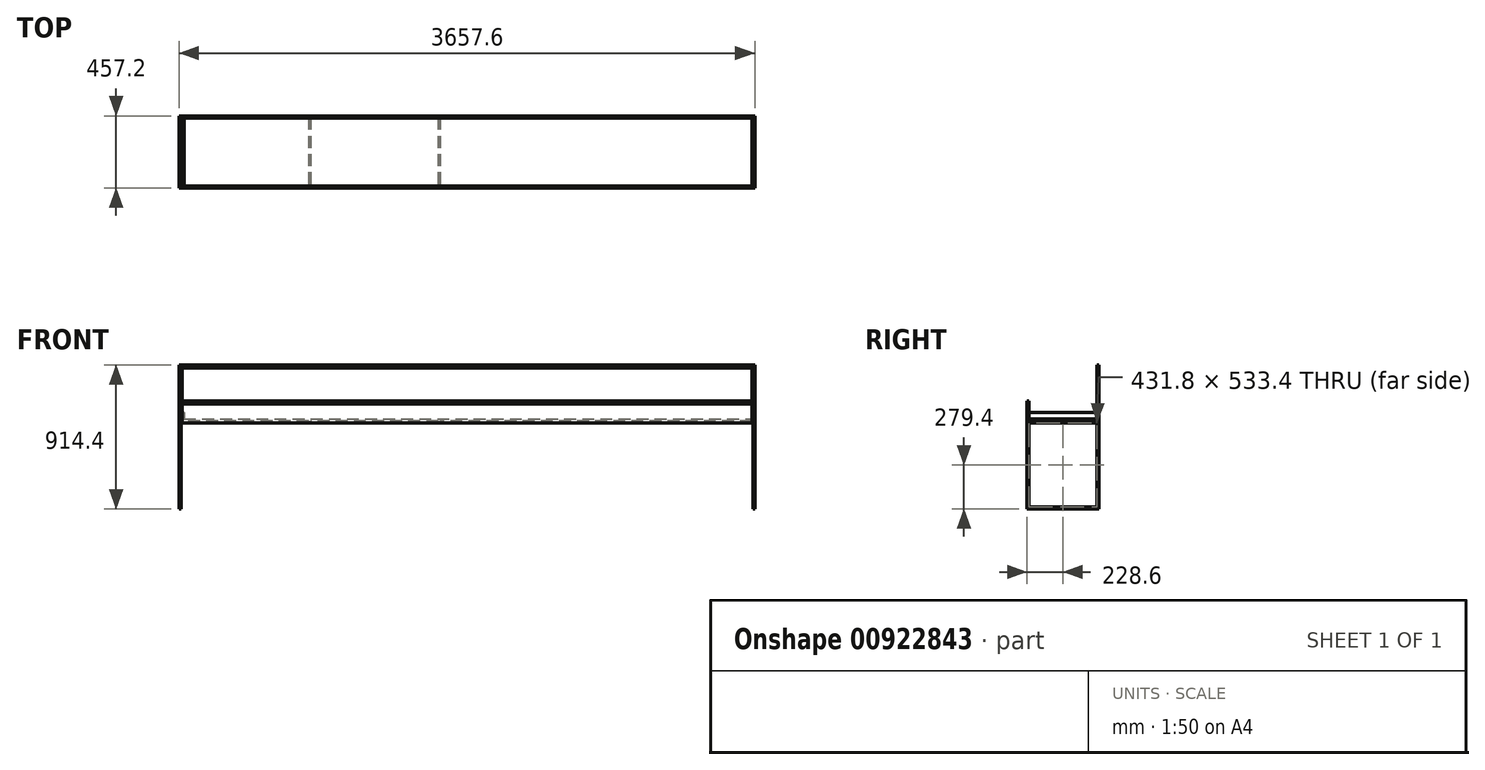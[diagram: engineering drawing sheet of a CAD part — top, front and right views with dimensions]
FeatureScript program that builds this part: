
annotation { "Feature Type Name" : "Feature", "Feature Type Description" : "" }
export const myFeature = defineFeature(function(context is Context, id is Id, definition is map)
    precondition{}
    {
        {
            var Q0;
            Q0=qCreatedBy(makeId("Front.planeOp"),FACE);
            var sketch = newSketch(context, id + "F0", { "sketchPlane" : qUnion([Q0])});
            skLineSegment(sketch, "E0.bottom", {"start": v(-2785.08, 0) * mm, "end": v(872.52, 0) * mm});
            skLineSegment(sketch, "E0.top", {"start": v(-2785.08, 914.4) * mm, "end": v(872.52, 914.4) * mm});
            skLineSegment(sketch, "E0.left", {"start": v(-2785.08, 0) * mm, "end": v(-2785.08, 914.4) * mm});
            skLineSegment(sketch, "E0.right", {"start": v(872.52, 0) * mm, "end": v(872.52, 914.4) * mm});
            skSolve(sketch);
        }
        {
            var Q0;
            Q0=makeQuery(id+"F0.imprint","IMPRINT",FACE,{"disambiguationData":[TD([[makeQuery(id+"F0.imprint","IMPRINT",EDGE,{"derivedFrom":sQuery(id+"F0.wireOp",EDGE,"E0.bottom")}),1.0]])]});
            extrude(context, id + "F1", {"entities" : qUnion([Q0]), "depth" : 457.2 * mm, "offsetDistance" : 30.48 * mm});
        }
        {
            var Q0;
            Q0=makeQuery(id+"F1.opExtrude","SWEPT_FACE",FACE,{"disambiguationData":[OSD([sQuery(id+"F0.wireOp",EDGE,"E0.left")])]});
            var sketch = newSketch(context, id + "F2", { "sketchPlane" : qUnion([Q0])});
            skLineSegment(sketch, "E1.bottom", {"start": v(457.2, 914.4) * mm, "end": v(12.7, 914.4) * mm});
            skLineSegment(sketch, "E1.top", {"start": v(444.5, 12.7) * mm, "end": v(12.7, 12.7) * mm});
            skLineSegment(sketch, "E1.left", {"start": v(444.5, 558.8) * mm, "end": v(444.5, 12.7) * mm});
            skLineSegment(sketch, "E1.right", {"start": v(12.7, 914.4) * mm, "end": v(12.7, 12.7) * mm});
            skLineSegment(sketch, "E2", {"start": v(444.5, 558.8) * mm, "end": v(457.2, 558.8) * mm});
            skLineSegment(sketch, "E3", {"start": v(457.2, 558.8) * mm, "end": v(457.2, 914.4) * mm});
            skSolve(sketch);
        }
        {
            var Q0;
            Q0 = qSketchRegion(id + "F2", true);
            extrude(context, id + "F3", {"entities" : qUnion([Q0]), "operationType" : NewBodyOperationType.REMOVE, "endBound" : BoundingType.UP_TO_NEXT, "oppositeDirection" : true, "depth" : 1914.14 * mm, "offsetDistance" : 30.48 * mm});
        }
        {
            var Q0;
            Q0=sQuery(id+"F0.wireOp",EDGE,"E0.top");
            cPoint(context, id + "F4", {"entities" : qUnion([Q0]), "parameter" : 0.5});
        }
        {
            var Q0;
            Q0 = qCreatedBy(id + "F4" ,VERTEX);
            var Q1;
            Q1=qCreatedBy(makeId("Right.planeOp"),FACE);
            cPlane(context, id + "F5", {"entities" : qUnion([Q0, Q1]), "cplaneType" : CPlaneType.PLANE_POINT, "offset" : 25.4 * mm, "width" : 152.4 * mm, "height" : 152.4 * mm});
        }
        {
            var Q0;
            Q0=qCreatedBy(id+"F5.planeOp",FACE);
            var sketch = newSketch(context, id + "F6", { "sketchPlane" : qUnion([Q0])});
            skLineSegment(sketch, "E4", {"start": v(178.18, 901.7) * mm, "end": v(-187, 901.7) * mm});
            skLineSegment(sketch, "E5", {"start": v(-187, 901.7) * mm, "end": v(-187, 546.1) * mm});
            skLineSegment(sketch, "E6", {"start": v(-187, 546.1) * mm, "end": v(-558.28, 546.1) * mm});
            skLineSegment(sketch, "E7", {"start": v(-558.28, 546.1) * mm, "end": v(-558.28, -48.09) * mm});
            skLineSegment(sketch, "E8", {"start": v(-558.28, -48.09) * mm, "end": v(178.18, -48.09) * mm});
            skLineSegment(sketch, "E9", {"start": v(178.18, -48.09) * mm, "end": v(178.18, 901.7) * mm});
            skSolve(sketch);
        }
        {
            var Q0;
            Q0 = qSketchRegion(id + "F6", true);
            var Q1;
            Q1=makeQuery(id+"F1.opExtrude","SWEPT_FACE",FACE,{"disambiguationData":[OSD([sQuery(id+"F0.wireOp",EDGE,"E0.left")])]});
            extrude(context, id + "F7", {"entities" : qUnion([Q0]), "operationType" : NewBodyOperationType.REMOVE, "endBound" : BoundingType.UP_TO_SURFACE, "oppositeDirection" : true, "depth" : 30.48 * mm, "endBoundEntityFace" : qUnion([Q1]), "hasOffset" : true, "offsetDistance" : 12.7 * mm});
        }
        {
            var Q0;
            Q0 = qSketchRegion(id + "F6", true);
            var Q1;
            Q1=makeQuery(id+"F1.opExtrude","SWEPT_FACE",FACE,{"disambiguationData":[OSD([sQuery(id+"F0.wireOp",EDGE,"E0.right")])]});
            extrude(context, id + "F8", {"entities" : qUnion([Q0]), "operationType" : NewBodyOperationType.REMOVE, "endBound" : BoundingType.UP_TO_SURFACE, "depth" : 30.48 * mm, "endBoundEntityFace" : qUnion([Q1]), "hasOffset" : true, "offsetDistance" : 12.7 * mm});
        }
        {
            var Q0;
            Q0=makeQuery(id+"F1.opExtrude","CAP_FACE",FACE,{"disambiguationData":[OSD([sQuery(id+"F0.wireOp",EDGE,"E0.bottom"),sQuery(id+"F0.wireOp",EDGE,"E0.top"),sQuery(id+"F0.wireOp",EDGE,"E0.left"),sQuery(id+"F0.wireOp",EDGE,"E0.right")])],"isStart":false});
            var sketch = newSketch(context, id + "F9", { "sketchPlane" : qUnion([Q0])});
            skLineSegment(sketch, "E10", {"start": v(-2785.08, 558.8) * mm, "end": v(-2785.08, 685.8) * mm});
            skLineSegment(sketch, "E11", {"start": v(-2785.08, 685.8) * mm, "end": v(872.52, 685.8) * mm});
            skLineSegment(sketch, "E12", {"start": v(872.52, 685.8) * mm, "end": v(872.52, 558.8) * mm});
            skLineSegment(sketch, "E13.0", {"start": v(859.82, 673.1) * mm, "end": v(859.82, 558.8) * mm});
            skLineSegment(sketch, "E13.1", {"start": v(-2772.38, 673.1) * mm, "end": v(859.82, 673.1) * mm});
            skLineSegment(sketch, "E13.2", {"start": v(-2772.38, 558.8) * mm, "end": v(-2772.38, 673.1) * mm});
            skLineSegment(sketch, "E14", {"start": v(-2785.08, 558.8) * mm, "end": v(-2772.38, 558.8) * mm});
            skLineSegment(sketch, "E15", {"start": v(859.82, 558.8) * mm, "end": v(872.52, 558.8) * mm});
            skSolve(sketch);
        }
        {
            var Q0;
            Q0 = qSketchRegion(id + "F9", true);
            var Q1;
            Q1=makeQuery(id+"F3.boolean.opBoolean","COPY",VERTEX,{"derivedFrom":makeQuery(id+"F3.opExtrude","CAP_VERTEX",VERTEX,{"disambiguationData":[OSD([sQuery(id+"F2.wireOp",EDGE,"E1.left"),sQuery(id+"F2.wireOp",EDGE,"E2")])],"isStart":true})});
            extrude(context, id + "F10", {"entities" : qUnion([Q0]), "operationType" : NewBodyOperationType.ADD, "endBound" : BoundingType.UP_TO_VERTEX, "oppositeDirection" : true, "depth" : 30.48 * mm, "endBoundEntityVertex" : qUnion([Q1]), "offsetDistance" : 30.48 * mm});
        }
        {
            var Q0;
            Q0=makeQuery(id+"F10.boolean.opBoolean","MERGE",FACE,{"derivedFrom":[makeQuery(id+"F1.opExtrude","SWEPT_FACE",FACE,{"disambiguationData":[OSD([sQuery(id+"F0.wireOp",EDGE,"E0.left")])]}),makeQuery(id+"F10.opExtrude","SWEPT_FACE",FACE,{"disambiguationData":[OSD([sQuery(id+"F9.wireOp",EDGE,"E10")])]})]});
            var sketch = newSketch(context, id + "F11", { "sketchPlane" : qUnion([Q0])});
            skLineSegment(sketch, "E16.bottom", {"start": v(0, 558.8) * mm, "end": v(12.7, 558.8) * mm});
            skLineSegment(sketch, "E16.top", {"start": v(0, 546.1) * mm, "end": v(12.7, 546.1) * mm});
            skLineSegment(sketch, "E16.left", {"start": v(0, 558.8) * mm, "end": v(0, 546.1) * mm});
            skLineSegment(sketch, "E16.right", {"start": v(12.7, 558.8) * mm, "end": v(12.7, 546.1) * mm});
            skSolve(sketch);
        }
        {
            var Q0;
            Q0 = qSketchRegion(id + "F11", true);
            var Q1;
            Q1=makeQuery(id+"F8.boolean.opBoolean","COPY",FACE,{"derivedFrom":makeQuery(id+"F8.opExtrude","CAP_FACE",FACE,{"disambiguationData":[OSD([sQuery(id+"F6.wireOp",EDGE,"E4"),sQuery(id+"F6.wireOp",EDGE,"E5"),sQuery(id+"F6.wireOp",EDGE,"E6"),sQuery(id+"F6.wireOp",EDGE,"E7"),sQuery(id+"F6.wireOp",EDGE,"E8"),sQuery(id+"F6.wireOp",EDGE,"E9")])],"isStart":false})});
            extrude(context, id + "F12", {"entities" : qUnion([Q0]), "operationType" : NewBodyOperationType.ADD, "endBound" : BoundingType.UP_TO_SURFACE, "oppositeDirection" : true, "depth" : 30.48 * mm, "endBoundEntityFace" : qUnion([Q1]), "offsetDistance" : 30.48 * mm});
        }
        {
            var Q0;
            Q0=makeQuery(id+"F10.boolean.opBoolean","MERGE",FACE,{"derivedFrom":[makeQuery(id+"F1.opExtrude","CAP_FACE",FACE,{"disambiguationData":[OSD([sQuery(id+"F0.wireOp",EDGE,"E0.bottom"),sQuery(id+"F0.wireOp",EDGE,"E0.top"),sQuery(id+"F0.wireOp",EDGE,"E0.left"),sQuery(id+"F0.wireOp",EDGE,"E0.right")])],"isStart":false}),makeQuery(id+"F10.opExtrude","CAP_FACE",FACE,{"disambiguationData":[OSD([sQuery(id+"F9.wireOp",EDGE,"E10"),sQuery(id+"F9.wireOp",EDGE,"E11"),sQuery(id+"F9.wireOp",EDGE,"E12"),sQuery(id+"F9.wireOp",EDGE,"E13.0"),sQuery(id+"F9.wireOp",EDGE,"E13.1"),sQuery(id+"F9.wireOp",EDGE,"E13.2"),sQuery(id+"F9.wireOp",EDGE,"E14"),sQuery(id+"F9.wireOp",EDGE,"E15")])],"isStart":true})]});
            var sketch = newSketch(context, id + "F13", { "sketchPlane" : qUnion([Q0])});
            skLineSegment(sketch, "E17.bottom", {"start": v(-2772.38, 546.1) * mm, "end": v(-2785.08, 546.1) * mm});
            skLineSegment(sketch, "E17.top", {"start": v(-2772.38, 558.8) * mm, "end": v(-2785.08, 558.8) * mm});
            skLineSegment(sketch, "E17.left", {"start": v(-2772.38, 546.1) * mm, "end": v(-2772.38, 558.8) * mm});
            skLineSegment(sketch, "E17.right", {"start": v(-2785.08, 546.1) * mm, "end": v(-2785.08, 558.8) * mm});
            skLineSegment(sketch, "E18.bottom", {"start": v(859.82, 558.8) * mm, "end": v(872.52, 558.8) * mm});
            skLineSegment(sketch, "E18.top", {"start": v(859.82, 546.1) * mm, "end": v(872.52, 546.1) * mm});
            skLineSegment(sketch, "E18.left", {"start": v(859.82, 558.8) * mm, "end": v(859.82, 546.1) * mm});
            skLineSegment(sketch, "E18.right", {"start": v(872.52, 558.8) * mm, "end": v(872.52, 546.1) * mm});
            skLineSegment(sketch, "E19.1.0.0", {"start": v(-1949.42, 558.8) * mm, "end": v(-1962.12, 558.8) * mm});
            skLineSegment(sketch, "E19.1.0.1", {"start": v(-1949.42, 546.1) * mm, "end": v(-1949.42, 558.8) * mm});
            skLineSegment(sketch, "E19.1.0.2", {"start": v(-1949.42, 546.1) * mm, "end": v(-1962.12, 546.1) * mm});
            skLineSegment(sketch, "E19.1.0.3", {"start": v(-1962.12, 546.1) * mm, "end": v(-1962.12, 558.8) * mm});
            skLineSegment(sketch, "E19.2.0.0", {"start": v(-1126.46, 558.8) * mm, "end": v(-1139.16, 558.8) * mm});
            skLineSegment(sketch, "E19.2.0.1", {"start": v(-1126.46, 546.1) * mm, "end": v(-1126.46, 558.8) * mm});
            skLineSegment(sketch, "E19.2.0.2", {"start": v(-1126.46, 546.1) * mm, "end": v(-1139.16, 546.1) * mm});
            skLineSegment(sketch, "E19.2.0.3", {"start": v(-1139.16, 546.1) * mm, "end": v(-1139.16, 558.8) * mm});
            skLineSegment(sketch, "E19.direction1", {"start": v(-2785.08, 558.8) * mm, "end": v(-1962.12, 558.8) * mm, "construction": true});
            skSolve(sketch);
        }
        {
            var Q0;
            Q0 = qSketchRegion(id + "F13", true);
            var Q1;
            Q1=makeQuery(id+"F12.boolean.opBoolean","MERGE",FACE,{"derivedFrom":[makeQuery(id+"F3.boolean.opBoolean","COPY",FACE,{"derivedFrom":makeQuery(id+"F3.opExtrude","SWEPT_FACE",FACE,{"disambiguationData":[OSD([sQuery(id+"F2.wireOp",EDGE,"E1.right")])]})}),makeQuery(id+"F12.opExtrude","SWEPT_FACE",FACE,{"disambiguationData":[OSD([sQuery(id+"F11.wireOp",EDGE,"E16.right")])]})]});
            extrude(context, id + "F14", {"entities" : qUnion([Q0]), "operationType" : NewBodyOperationType.ADD, "endBound" : BoundingType.UP_TO_SURFACE, "oppositeDirection" : true, "depth" : 30.48 * mm, "endBoundEntityFace" : qUnion([Q1]), "offsetDistance" : 30.48 * mm});
        }
        {
            var Q0;
            Q0=qCreatedBy(id+"F5.planeOp",FACE);
            var sketch = newSketch(context, id + "F15", { "sketchPlane" : qUnion([Q0])});
            skLineSegment(sketch, "E20", {"start": v(0, 895.35) * mm, "end": v(0, 558.8) * mm});
            skLineSegment(sketch, "E21", {"start": v(0, 558.8) * mm, "end": v(-457.2, 558.8) * mm});
            skLineSegment(sketch, "E22", {"start": v(-457.2, 558.8) * mm, "end": v(-457.2, 666.75) * mm});
            skLineSegment(sketch, "E23", {"start": v(-457.2, 666.75) * mm, "end": v(-444.5, 666.75) * mm});
            skLineSegment(sketch, "E24", {"start": v(-444.5, 666.75) * mm, "end": v(-444.5, 571.5) * mm});
            skLineSegment(sketch, "E25", {"start": v(-444.5, 571.5) * mm, "end": v(-12.7, 571.5) * mm});
            skLineSegment(sketch, "E26", {"start": v(-12.7, 571.5) * mm, "end": v(-12.7, 895.35) * mm});
            skLineSegment(sketch, "E27", {"start": v(-12.7, 895.35) * mm, "end": v(0, 895.35) * mm});
            skSolve(sketch);
        }
        {
            var Q0;
            Q0 = qSketchRegion(id + "F15", true);
            var Q1;
            Q1=makeQuery(id+"F10.opExtrude","SWEPT_FACE",FACE,{"disambiguationData":[OSD([sQuery(id+"F9.wireOp",EDGE,"E13.2")])]});
            extrude(context, id + "F16", {"entities" : qUnion([Q0]), "endBound" : BoundingType.UP_TO_SURFACE, "oppositeDirection" : true, "depth" : 30.48 * mm, "endBoundEntityFace" : qUnion([Q1]), "hasOffset" : true, "offsetDistance" : 6.35 * mm});
        }
        {
            var Q0;
            Q0 = qSketchRegion(id + "F15", true);
            var Q1;
            {var subQ0=sQuery(id+"F6.wireOp",EDGE,"E4");Q1=makeQuery(id+"F12.boolean.opBoolean","SPLIT",FACE,{"disambiguationData":[TD([makeQuery(id+"F7.boolean.opBoolean","COPY",FACE,{"derivedFrom":makeQuery(id+"F7.opExtrude","SWEPT_FACE",FACE,{"disambiguationData":[OSD([subQ0])]})})])],"derivedFrom":makeQuery(id+"F8.boolean.opBoolean","COPY",FACE,{"derivedFrom":makeQuery(id+"F8.opExtrude","CAP_FACE",FACE,{"disambiguationData":[OSD([subQ0,sQuery(id+"F6.wireOp",EDGE,"E5"),sQuery(id+"F6.wireOp",EDGE,"E6"),sQuery(id+"F6.wireOp",EDGE,"E7"),sQuery(id+"F6.wireOp",EDGE,"E8"),sQuery(id+"F6.wireOp",EDGE,"E9")])],"isStart":false})})});}
            extrude(context, id + "F17", {"entities" : qUnion([Q0]), "operationType" : NewBodyOperationType.ADD, "endBound" : BoundingType.UP_TO_SURFACE, "depth" : 30.48 * mm, "endBoundEntityFace" : qUnion([Q1]), "hasOffset" : true, "offsetDistance" : 6.35 * mm});
        }
        {
            var Q0;
            Q0=makeQuery(id+"F16.opExtrude","CAP_FACE",FACE,{"disambiguationData":[OSD([sQuery(id+"F15.wireOp",EDGE,"E20"),sQuery(id+"F15.wireOp",EDGE,"E21"),sQuery(id+"F15.wireOp",EDGE,"E22"),sQuery(id+"F15.wireOp",EDGE,"E23"),sQuery(id+"F15.wireOp",EDGE,"E24"),sQuery(id+"F15.wireOp",EDGE,"E25"),sQuery(id+"F15.wireOp",EDGE,"E26"),sQuery(id+"F15.wireOp",EDGE,"E27")])],"isStart":false});
            var sketch = newSketch(context, id + "F18", { "sketchPlane" : qUnion([Q0])});
            skLineSegment(sketch, "E28.bottom", {"start": v(457.2, 558.8) * mm, "end": v(0, 558.8) * mm});
            skLineSegment(sketch, "E28.top", {"start": v(457.2, 612.78) * mm, "end": v(0, 612.78) * mm});
            skLineSegment(sketch, "E28.left", {"start": v(457.2, 558.8) * mm, "end": v(457.2, 666.75) * mm});
            skLineSegment(sketch, "E28.right", {"start": v(0, 558.8) * mm, "end": v(0, 612.78) * mm});
            skSolve(sketch);
        }
        {
            var Q0;
            Q0 = qSketchRegion(id + "F18", true);
            extrude(context, id + "F19", {"entities" : qUnion([Q0]), "operationType" : NewBodyOperationType.ADD, "oppositeDirection" : true, "depth" : 12.7 * mm, "offsetDistance" : 30.48 * mm});
        }
    });
